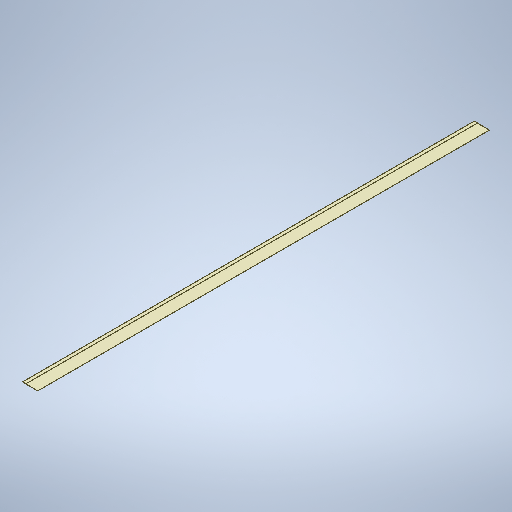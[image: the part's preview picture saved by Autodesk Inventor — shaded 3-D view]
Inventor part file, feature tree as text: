
AUTODESK INVENTOR PART (.ipt)
format: ipt  version: 2025 (Build 290162010, 162A)  size: 262,144 bytes
history: native  units: in
note: dims shown in document units (in); Inventor stores cm internally (conversion verified against a paired STEP export)
features: extrude x1, sketch x1
ambient origin geometry x8: Origin, YZ Plane, XZ Plane, XY Plane, X Axis, Y Axis, Z Axis, Center Point
bodies: Body1 (feature_tree)
feature tree (2):
  extrude  "Extrusion2"  Depth=0.125in
  sketch  "Sketch1"  dims[d0=2.0in d1=0.125in d2=0.125in d3=0.125in d4=0.125in d8=292.512in d9=0.0in d10=7.806in]
